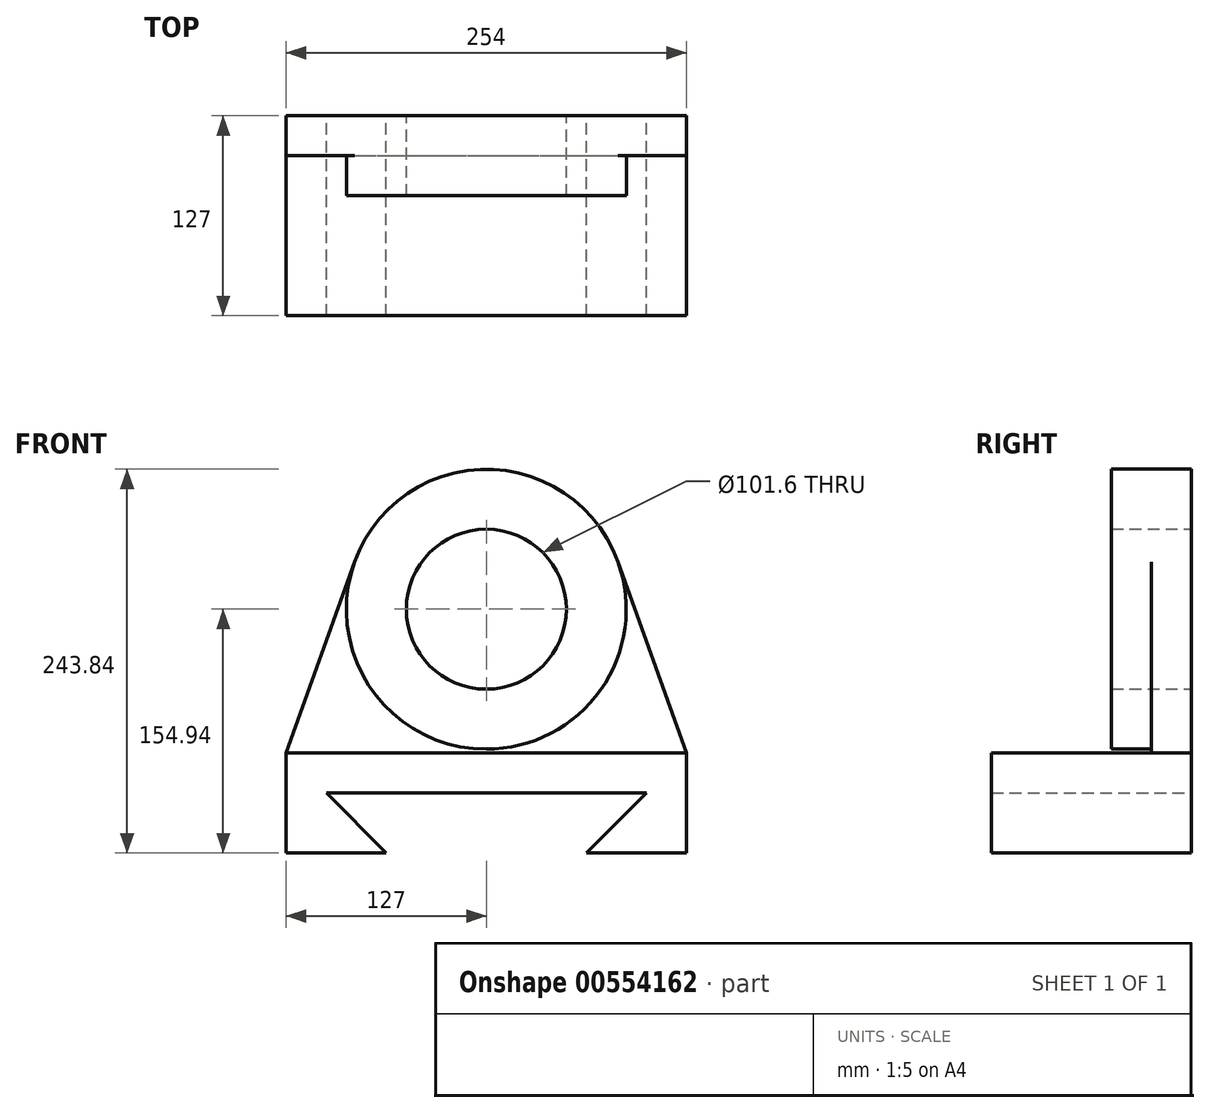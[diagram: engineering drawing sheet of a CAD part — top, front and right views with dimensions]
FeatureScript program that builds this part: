
annotation { "Feature Type Name" : "Feature", "Feature Type Description" : "" }
export const myFeature = defineFeature(function(context is Context, id is Id, definition is map)
    precondition{}
    {
        {
            var Q0;
            Q0=qCreatedBy(makeId("Front.planeOp"),FACE);
            var sketch = newSketch(context, id + "F0", { "sketchPlane" : qUnion([Q0])});
            skLineSegment(sketch, "E0", {"start": v(0, 0) * mm, "end": v(254, 0) * mm});
            skLineSegment(sketch, "E1", {"start": v(0, 0) * mm, "end": v(0, -63.5) * mm});
            skLineSegment(sketch, "E2", {"start": v(254, 0) * mm, "end": v(254, -63.5) * mm});
            skLineSegment(sketch, "E3", {"start": v(254, -63.5) * mm, "end": v(190.5, -63.5) * mm});
            skLineSegment(sketch, "E4", {"start": v(0, -63.5) * mm, "end": v(63.5, -63.5) * mm});
            skLineSegment(sketch, "E5", {"start": v(63.5, -63.5) * mm, "end": v(25.4, -25.4) * mm});
            skLineSegment(sketch, "E6", {"start": v(190.5, -63.5) * mm, "end": v(228.6, -25.4) * mm});
            skLineSegment(sketch, "E7", {"start": v(25.4, -25.4) * mm, "end": v(228.6, -25.4) * mm});
            skCircle(sketch, "E8", {"center": v(127, 91.44) * mm, "radius": 50.8 * mm});
            skCircle(sketch, "E9", {"center": v(127, 91.44) * mm, "radius": 88.9 * mm});
            skLineSegment(sketch, "E10", {"start": v(0, 0) * mm, "end": v(43.27, 121.3) * mm});
            skLineSegment(sketch, "E11", {"start": v(254, 0) * mm, "end": v(210.73, 121.3) * mm});
            skSolve(sketch);
        }
        {
            var Q0;
            Q0=makeQuery(id+"F0.imprint","IMPRINT",FACE,{"disambiguationData":[TD([[makeQuery(id+"F0.imprint","IMPRINT",EDGE,{"derivedFrom":sQuery(id+"F0.wireOp",EDGE,"E0")}),-1.0]])]});
            extrude(context, id + "F1", {"entities" : qUnion([Q0]), "depth" : 127 * mm, "offsetDistance" : 25.4 * mm});
        }
        {
            var Q0;
            Q0=makeQuery(id+"F0.imprint","IMPRINT",FACE,{"disambiguationData":[TD([[makeQuery(id+"F0.imprint","IMPRINT",EDGE,{"derivedFrom":sQuery(id+"F0.wireOp",EDGE,"E0")}),1.0]])]});
            extrude(context, id + "F2", {"entities" : qUnion([Q0]), "operationType" : NewBodyOperationType.ADD, "depth" : 25.4 * mm, "offsetDistance" : 25.4 * mm});
        }
        {
            var Q0;
            Q0=makeQuery(id+"F0.imprint","IMPRINT",FACE,{"disambiguationData":[TD([[makeQuery(id+"F0.imprint","IMPRINT",EDGE,{"derivedFrom":sQuery(id+"F0.wireOp",EDGE,"E8")}),-1.0]])]});
            extrude(context, id + "F3", {"entities" : qUnion([Q0]), "operationType" : NewBodyOperationType.ADD, "depth" : 50.8 * mm, "offsetDistance" : 25.4 * mm});
        }
    });
